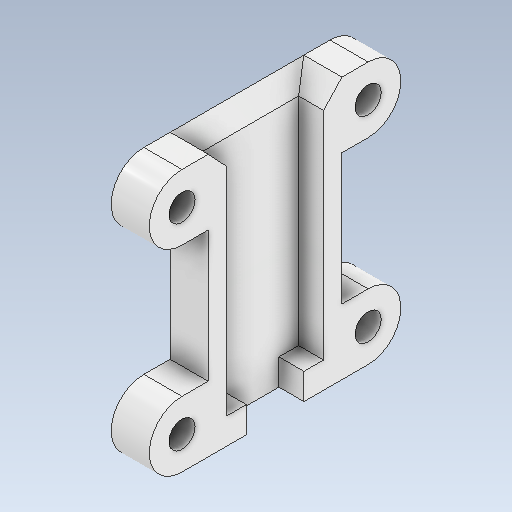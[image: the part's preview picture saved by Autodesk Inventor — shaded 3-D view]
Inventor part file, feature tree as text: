
AUTODESK INVENTOR PART (.ipt)
format: ipt  version: 2020 (Build 240168000, 168)  size: 181,248 bytes
history: native  units: in
note: dims shown in document units (in); Inventor stores cm internally (conversion verified against a paired STEP export)
features: sketch x6, other x3
ambient origin geometry x8: Origin, YZ Plane, XZ Plane, XY Plane, X Axis, Y Axis, Z Axis, Center Point
bodies: Solid1 (feature_tree)
feature tree (9):
  other  "PistonCasingTop.ipt"
  other  "Solid1::PistonCasingTop.ipt"
  other  "TaggingFeature1"
  sketch  "Sketch1"  dims[d0=0.3937in]
  sketch  "Sketch2"
  sketch  "Sketch3"
  sketch  "Sketch4"
  sketch  "Sketch5"
  sketch  "Sketch6"
